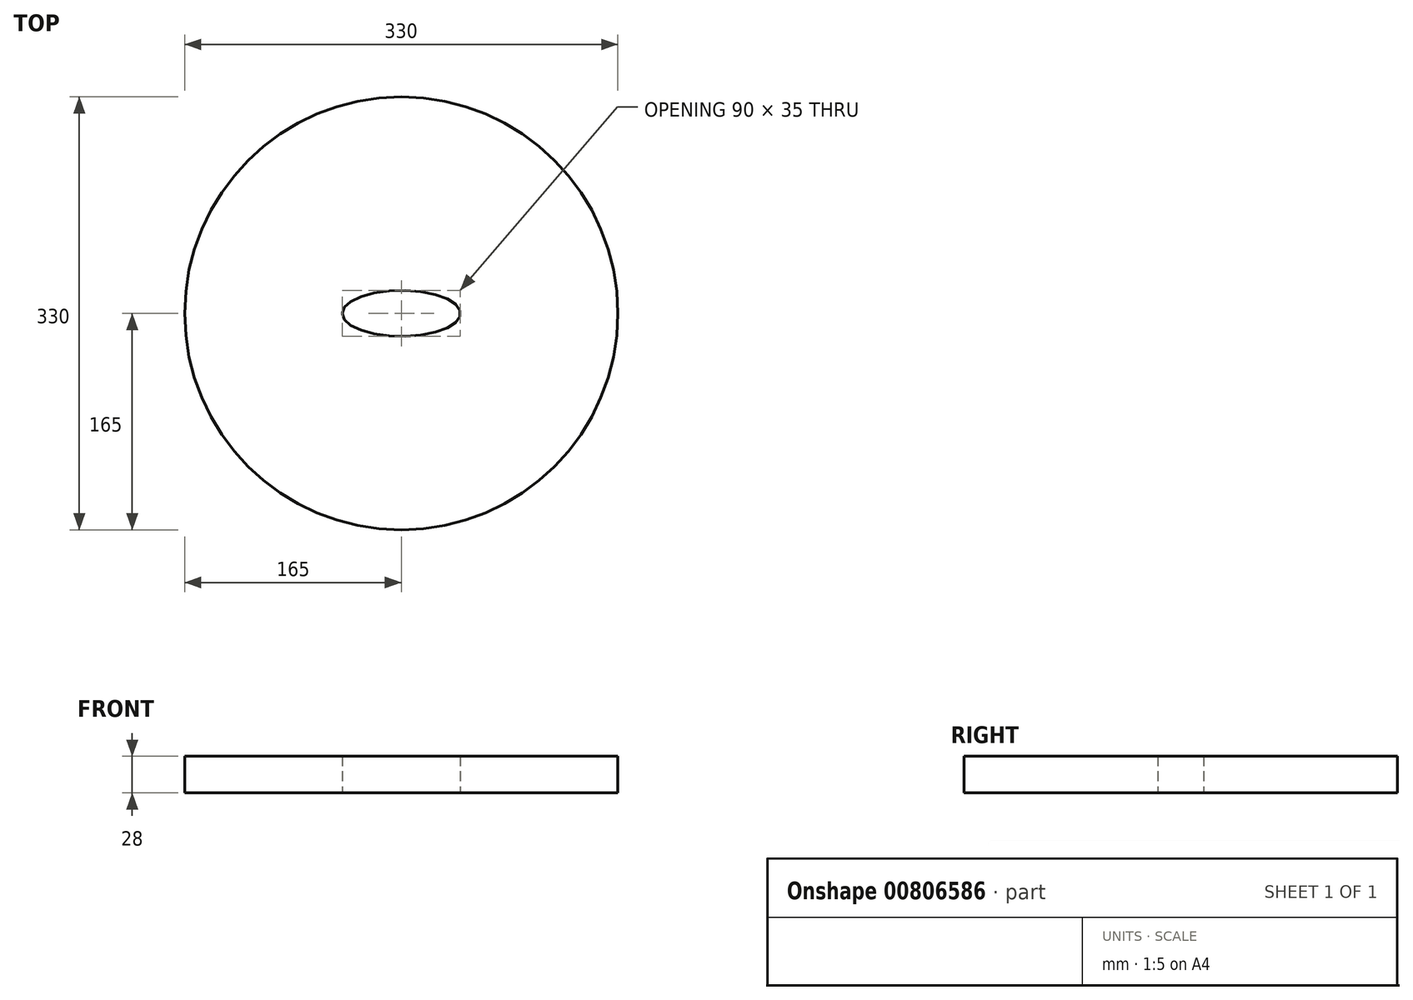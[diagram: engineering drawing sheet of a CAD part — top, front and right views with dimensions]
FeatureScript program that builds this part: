
annotation { "Feature Type Name" : "Feature", "Feature Type Description" : "" }
export const myFeature = defineFeature(function(context is Context, id is Id, definition is map)
    precondition{}
    {
        {
            var Q0;
            Q0=qCreatedBy(makeId("Top.planeOp"),FACE);
            var sketch = newSketch(context, id + "F0", { "sketchPlane" : qUnion([Q0])});
            skCircle(sketch, "E0", {"center": v(165, 165) * mm, "radius": 165 * mm});
            skLineSegment(sketch, "E1", {"start": v(0, 0) * mm, "end": v(0, 350) * mm, "construction": true});
            skLineSegment(sketch, "E2", {"start": v(0, 0) * mm, "end": v(350, 0) * mm, "construction": true});
            skEllipse(sketch, "E3", {"center": v(165, 165) * mm, "majorRadius": 45 * mm, "minorRadius": 17.5 * mm, "majorAxis": v(-1, 0)});
            skSolve(sketch);
        }
        {
            var Q0;
            Q0 = qSketchRegion(id + "F0", true);
            extrude(context, id + "F1", {"entities" : qUnion([Q0]), "depth" : 28 * mm, "offsetDistance" : 25 * mm});
        }
    });
